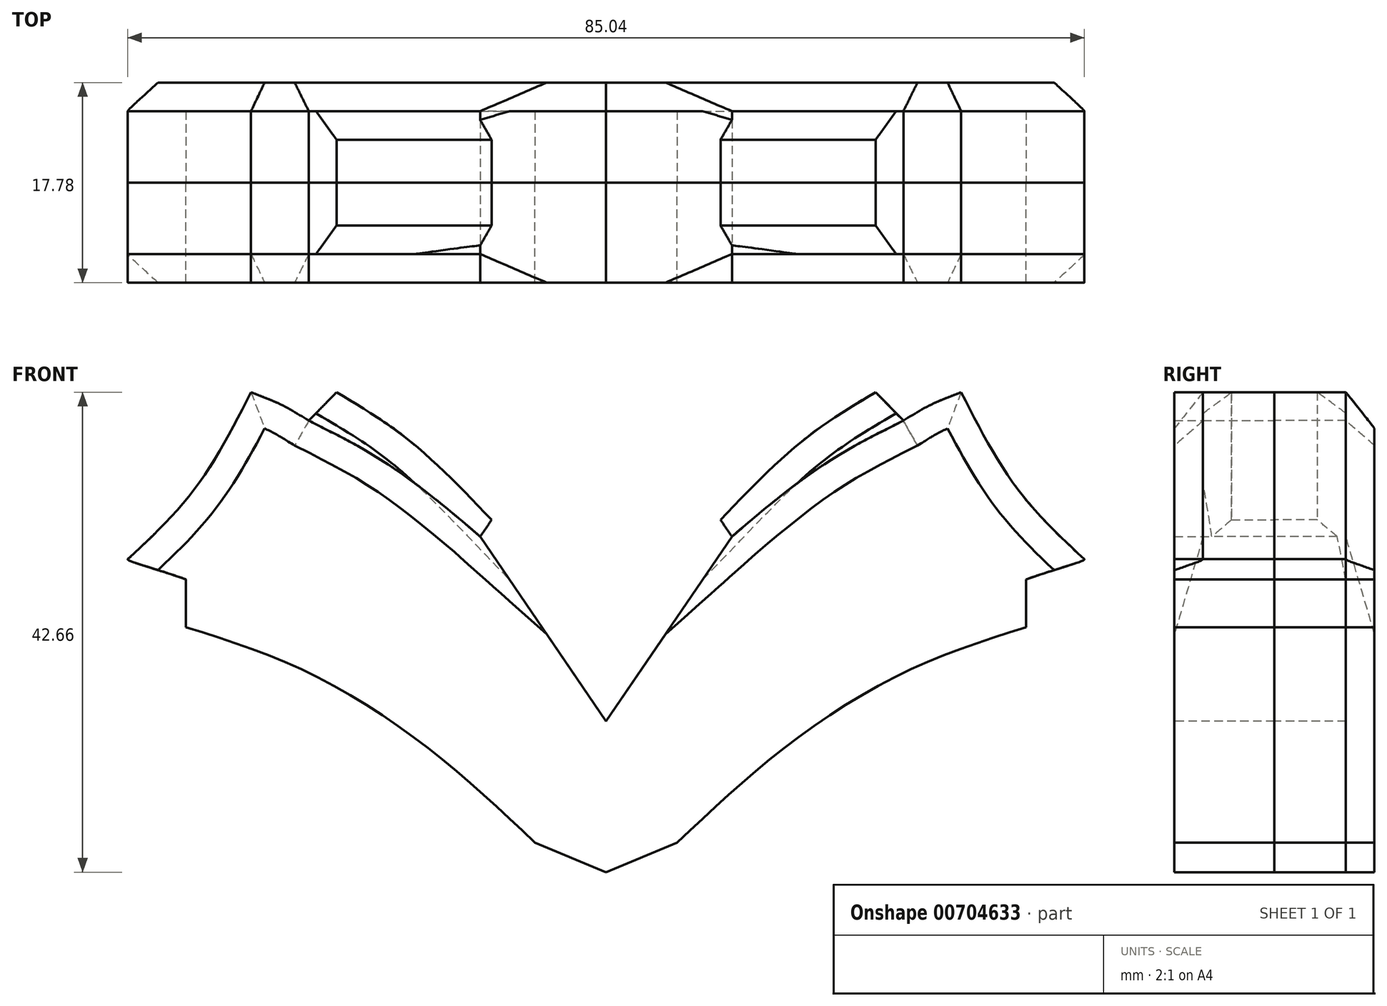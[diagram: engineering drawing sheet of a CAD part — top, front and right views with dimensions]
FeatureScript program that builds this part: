
annotation { "Feature Type Name" : "Feature", "Feature Type Description" : "" }
export const myFeature = defineFeature(function(context is Context, id is Id, definition is map)
    precondition{}
    {
        {
            var Q0;
            Q0=qCreatedBy(makeId("Front.planeOp"),FACE);
            var sketch = newSketch(context, id + "F0", { "sketchPlane" : qUnion([Q0])});
            skFitSpline(sketch, "E0", {"points": [v(-18.66, -145.03) * mm, v(-12.41, -140.25) * mm, v(-7.43, -132.73) * mm], "startDerivative": vector(13.73, 8.78) * mm, "endDerivative": vector(8.77, 15.73) * mm});
            skFitSpline(sketch, "E1", {"points": [v(0, -156.5) * mm, v(-5.42, -154.99) * mm, v(-8.85, -151.2) * mm], "startDerivative": vector(-11.5, 1.7) * mm, "endDerivative": vector(-6.16, 8.95) * mm});
            skFitSpline(sketch, "E2", {"points": [v(-6.32, -27.2) * mm, v(-15.28, -19.21) * mm, v(-26.43, -12.1) * mm, v(-37.33, -8.05) * mm], "startDerivative": vector(-25.96, 24.63) * mm, "endDerivative": vector(-33.62, 10.63) * mm});
            skFitSpline(sketch, "E3", {"points": [v(-37.33, -3.8) * mm, v(-39.84, -2.96) * mm, v(-42.51, -2.04) * mm, v(-42.5, -2) * mm], "startDerivative": vector(-4.66, 1.6) * mm, "endDerivative": vector(0.46, 0.6) * mm});
            skFitSpline(sketch, "E4", {"points": [v(-42.5, -2) * mm, v(-36.56, 4.25) * mm, v(-31.56, 12.84) * mm], "startDerivative": vector(12.98, 12.08) * mm, "endDerivative": vector(8.97, 17.54) * mm});
            skFitSpline(sketch, "E5", {"points": [v(-31.56, 12.84) * mm, v(-28.75, 11.67) * mm, v(-26.43, 10.32) * mm], "startDerivative": vector(5.62, -2.14) * mm, "endDerivative": vector(4.63, -2.93) * mm});
            skFitSpline(sketch, "E6", {"points": [v(-23.95, 12.84) * mm, v(-17.54, 8.59) * mm, v(-10.17, 1.5) * mm], "startDerivative": vector(13.82, -8.22) * mm, "endDerivative": vector(13.74, -14.33) * mm});
            skLineSegment(sketch, "E7", {"start": v(-10.17, 1.5) * mm, "end": v(0, 17.06) * mm});
            skLineSegment(sketch, "E8", {"start": v(0, 17.06) * mm, "end": v(0, 9.54) * mm});
            skLineSegment(sketch, "E9", {"start": v(0, 9.54) * mm, "end": v(0, 17.06) * mm});
            skLineSegment(sketch, "E10", {"start": v(-37.33, -3.8) * mm, "end": v(-37.33, -8.05) * mm});
            skLineSegment(sketch, "E11", {"start": v(-23.95, 12.84) * mm, "end": v(-26.43, 10.32) * mm});
            skLineSegment(sketch, "E12", {"start": v(-6.32, -27.2) * mm, "end": v(0, -29.82) * mm});
            skLineSegment(sketch, "E13", {"start": v(0, -29.82) * mm, "end": v(-6.32, -27.2) * mm});
            skLineSegment(sketch, "E14", {"start": v(-7.43, -132.73) * mm, "end": v(-4.54, -130.41) * mm});
            skLineSegment(sketch, "E15", {"start": v(-4.54, -130.41) * mm, "end": v(0, -130.41) * mm});
            skLineSegment(sketch, "E16", {"start": v(0, -130.41) * mm, "end": v(-4.54, -130.41) * mm});
            skLineSegment(sketch, "E17", {"start": v(-8.85, -151.2) * mm, "end": v(-10.72, -152.9) * mm});
            skLineSegment(sketch, "E18", {"start": v(-10.72, -152.9) * mm, "end": v(-18.24, -148.4) * mm});
            skLineSegment(sketch, "E19", {"start": v(-18.24, -148.4) * mm, "end": v(-18.66, -145.03) * mm});
            skLineSegment(sketch, "E20.MirrorCS", {"start": v(10.17, 1.5) * mm, "end": v(0, 17.06) * mm});
            skFitSpline(sketch, "E21.MirrorCS", {"points": [v(23.95, 12.84) * mm, v(17.54, 8.59) * mm, v(10.17, 1.5) * mm], "startDerivative": vector(-13.82, -8.22) * mm, "endDerivative": vector(-13.74, -14.33) * mm});
            skLineSegment(sketch, "E22.MirrorCS", {"start": v(23.95, 12.84) * mm, "end": v(26.43, 10.32) * mm});
            skFitSpline(sketch, "E23.MirrorCS", {"points": [v(31.56, 12.84) * mm, v(28.75, 11.67) * mm, v(26.43, 10.32) * mm], "startDerivative": vector(-5.62, -2.14) * mm, "endDerivative": vector(-4.63, -2.93) * mm});
            skFitSpline(sketch, "E24.MirrorCS", {"points": [v(42.5, -2) * mm, v(36.56, 4.25) * mm, v(31.56, 12.84) * mm], "startDerivative": vector(-12.98, 12.08) * mm, "endDerivative": vector(-8.97, 17.54) * mm});
            skFitSpline(sketch, "E25.MirrorCS", {"points": [v(37.33, -3.8) * mm, v(39.84, -2.96) * mm, v(42.51, -2.04) * mm, v(42.5, -2) * mm], "startDerivative": vector(4.66, 1.6) * mm, "endDerivative": vector(-0.46, 0.6) * mm});
            skLineSegment(sketch, "E26.MirrorCS", {"start": v(37.33, -3.8) * mm, "end": v(37.33, -8.05) * mm});
            skFitSpline(sketch, "E27.MirrorCS", {"points": [v(6.32, -27.2) * mm, v(15.28, -19.21) * mm, v(26.43, -12.1) * mm, v(37.33, -8.05) * mm], "startDerivative": vector(25.96, 24.63) * mm, "endDerivative": vector(33.62, 10.63) * mm});
            skLineSegment(sketch, "E28.MirrorCS", {"start": v(6.32, -27.2) * mm, "end": v(0, -29.82) * mm});
            skLineSegment(sketch, "E29.MirrorCS", {"start": v(0, -130.41) * mm, "end": v(4.54, -130.41) * mm});
            skLineSegment(sketch, "E30.MirrorCS", {"start": v(7.43, -132.73) * mm, "end": v(4.54, -130.41) * mm});
            skFitSpline(sketch, "E31.MirrorCS", {"points": [v(18.66, -145.03) * mm, v(12.41, -140.25) * mm, v(7.43, -132.73) * mm], "startDerivative": vector(-13.73, 8.78) * mm, "endDerivative": vector(-8.77, 15.73) * mm});
            skLineSegment(sketch, "E32.MirrorCS", {"start": v(18.24, -148.4) * mm, "end": v(18.66, -145.03) * mm});
            skLineSegment(sketch, "E33.MirrorCS", {"start": v(10.72, -152.9) * mm, "end": v(18.24, -148.4) * mm});
            skLineSegment(sketch, "E34.MirrorCS", {"start": v(8.85, -151.2) * mm, "end": v(10.72, -152.9) * mm});
            skFitSpline(sketch, "E35.MirrorCS", {"points": [v(0, -156.5) * mm, v(5.42, -154.99) * mm, v(8.85, -151.2) * mm], "startDerivative": vector(11.5, 1.7) * mm, "endDerivative": vector(6.16, 8.95) * mm});
            skSolve(sketch);
        }
        {
            var Q0;
            Q0=makeQuery(id+"F0.imprint","IMPRINT",FACE,{"disambiguationData":[TD([[makeQuery(id+"F0.imprint","IMPRINT",EDGE,{"derivedFrom":sQuery(id+"F0.wireOp",EDGE,"E2")}),-1.0]])]});
            var Q1;
            Q1=makeQuery(id+"F0.imprint","IMPRINT",FACE,{"disambiguationData":[TD([[makeQuery(id+"F0.imprint","IMPRINT",EDGE,{"derivedFrom":sQuery(id+"F0.wireOp",EDGE,"E0")}),-1.0]])]});
            extrude(context, id + "F1", {"entities" : qUnion([Q0, Q1]), "depth" : 6.35 * mm, "offsetDistance" : 25.4 * mm});
        }
        {
            var Q0;
            Q0=makeQuery(id+"F1.opExtrude","CAP_FACE",FACE,{"disambiguationData":[OSD([sQuery(id+"F0.wireOp",EDGE,"E2"),sQuery(id+"F0.wireOp",EDGE,"E3"),sQuery(id+"F0.wireOp",EDGE,"E4"),sQuery(id+"F0.wireOp",EDGE,"E5"),sQuery(id+"F0.wireOp",EDGE,"E6"),sQuery(id+"F0.wireOp",EDGE,"E7"),sQuery(id+"F0.wireOp",EDGE,"E10"),sQuery(id+"F0.wireOp",EDGE,"E11"),sQuery(id+"F0.wireOp",EDGE,"E13"),sQuery(id+"F0.wireOp",EDGE,"E20.MirrorCS"),sQuery(id+"F0.wireOp",EDGE,"E21.MirrorCS"),sQuery(id+"F0.wireOp",EDGE,"E22.MirrorCS"),sQuery(id+"F0.wireOp",EDGE,"E23.MirrorCS"),sQuery(id+"F0.wireOp",EDGE,"E24.MirrorCS"),sQuery(id+"F0.wireOp",EDGE,"E25.MirrorCS"),sQuery(id+"F0.wireOp",EDGE,"E26.MirrorCS"),sQuery(id+"F0.wireOp",EDGE,"E27.MirrorCS"),sQuery(id+"F0.wireOp",EDGE,"E28.MirrorCS")])],"isStart":true});
            var Q1;
            Q1=makeQuery(id+"F1.opExtrude","CAP_FACE",FACE,{"disambiguationData":[OSD([sQuery(id+"F0.wireOp",EDGE,"E0"),sQuery(id+"F0.wireOp",EDGE,"E1"),sQuery(id+"F0.wireOp",EDGE,"E14"),sQuery(id+"F0.wireOp",EDGE,"E16"),sQuery(id+"F0.wireOp",EDGE,"E17"),sQuery(id+"F0.wireOp",EDGE,"E18"),sQuery(id+"F0.wireOp",EDGE,"E19"),sQuery(id+"F0.wireOp",EDGE,"E29.MirrorCS"),sQuery(id+"F0.wireOp",EDGE,"E30.MirrorCS"),sQuery(id+"F0.wireOp",EDGE,"E31.MirrorCS"),sQuery(id+"F0.wireOp",EDGE,"E32.MirrorCS"),sQuery(id+"F0.wireOp",EDGE,"E33.MirrorCS"),sQuery(id+"F0.wireOp",EDGE,"E34.MirrorCS"),sQuery(id+"F0.wireOp",EDGE,"E35.MirrorCS")])],"isStart":true});
            extrude(context, id + "F2", {"entities" : qUnion([Q0, Q1]), "depth" : 6.35 * mm, "offsetDistance" : 25.4 * mm});
        }
        {
            var Q0;
            Q0=makeQuery(id+"F1.opExtrude","CAP_FACE",FACE,{"disambiguationData":[OSD([sQuery(id+"F0.wireOp",EDGE,"E2"),sQuery(id+"F0.wireOp",EDGE,"E3"),sQuery(id+"F0.wireOp",EDGE,"E4"),sQuery(id+"F0.wireOp",EDGE,"E5"),sQuery(id+"F0.wireOp",EDGE,"E6"),sQuery(id+"F0.wireOp",EDGE,"E7"),sQuery(id+"F0.wireOp",EDGE,"E10"),sQuery(id+"F0.wireOp",EDGE,"E11"),sQuery(id+"F0.wireOp",EDGE,"E13"),sQuery(id+"F0.wireOp",EDGE,"E20.MirrorCS"),sQuery(id+"F0.wireOp",EDGE,"E21.MirrorCS"),sQuery(id+"F0.wireOp",EDGE,"E22.MirrorCS"),sQuery(id+"F0.wireOp",EDGE,"E23.MirrorCS"),sQuery(id+"F0.wireOp",EDGE,"E24.MirrorCS"),sQuery(id+"F0.wireOp",EDGE,"E25.MirrorCS"),sQuery(id+"F0.wireOp",EDGE,"E26.MirrorCS"),sQuery(id+"F0.wireOp",EDGE,"E27.MirrorCS"),sQuery(id+"F0.wireOp",EDGE,"E28.MirrorCS")])],"isStart":false});
            var sketch = newSketch(context, id + "F3", { "sketchPlane" : qUnion([Q0])});
            skFitSpline(sketch, "E36", {"points": [v(-26.43, 10.32) * mm, v(-20.88, 7.37) * mm, v(-15.82, 3.86) * mm, v(-11.19, 0) * mm, v(-9.86, -1.24) * mm], "startDerivative": vector(19.99, -10.01) * mm, "endDerivative": vector(7.2, -6.92) * mm});
            skLineSegment(sketch, "E37", {"start": v(-9.86, -1.24) * mm, "end": v(0, -16.46) * mm});
            skLineSegment(sketch, "E38.MirrorCS", {"start": v(9.86, -1.24) * mm, "end": v(0, -16.46) * mm});
            skFitSpline(sketch, "E39.MirrorCS", {"points": [v(26.43, 10.32) * mm, v(20.88, 7.37) * mm, v(15.82, 3.86) * mm, v(11.19, 0) * mm, v(9.86, -1.24) * mm], "startDerivative": vector(-19.99, -10.01) * mm, "endDerivative": vector(-7.2, -6.92) * mm});
            skLineSegment(sketch, "E40", {"start": v(-10.17, 1.5) * mm, "end": v(-11.19, 0) * mm});
            skLineSegment(sketch, "E41", {"start": v(10.17, 1.5) * mm, "end": v(11.19, 0) * mm});
            skSolve(sketch);
        }
        {
            var Q0;
            {var subQ7=sQuery(id+"F3.wireOp",EDGE,"E37");Q0=makeQuery(id+"F3.imprint","IMPRINT",FACE,{"disambiguationData":[TD([[makeQuery(id+"F3.imprint","IMPRINT",EDGE,{"derivedFrom":subQ7}),-1.0]])]});}
            var Q1;
            {var subQ3=sQuery(id+"F3.wireOp",EDGE,"E37");Q1=makeQuery(id+"F3.imprint","IMPRINT",FACE,{"disambiguationData":[TD([[makeQuery(id+"F3.imprint","IMPRINT",EDGE,{"derivedFrom":subQ3}),1.0]])]});}
            extrude(context, id + "F4", {"entities" : qUnion([Q0, Q1]), "operationType" : NewBodyOperationType.ADD, "depth" : 2.54 * mm, "offsetDistance" : 25.4 * mm});
        }
        {
            var Q0;
            Q0=makeQuery(id+"F4.opExtrude","CAP_FACE",FACE,{"disambiguationData":[OSD([sQuery(id+"F0.wireOp",EDGE,"E2"),sQuery(id+"F0.wireOp",EDGE,"E3"),sQuery(id+"F0.wireOp",EDGE,"E4"),sQuery(id+"F0.wireOp",EDGE,"E5"),sQuery(id+"F0.wireOp",EDGE,"E7"),sQuery(id+"F0.wireOp",EDGE,"E10"),sQuery(id+"F0.wireOp",EDGE,"E13"),sQuery(id+"F0.wireOp",EDGE,"E20.MirrorCS"),sQuery(id+"F0.wireOp",EDGE,"E23.MirrorCS"),sQuery(id+"F0.wireOp",EDGE,"E24.MirrorCS"),sQuery(id+"F0.wireOp",EDGE,"E25.MirrorCS"),sQuery(id+"F0.wireOp",EDGE,"E26.MirrorCS"),sQuery(id+"F0.wireOp",EDGE,"E27.MirrorCS"),sQuery(id+"F0.wireOp",EDGE,"E28.MirrorCS"),sQuery(id+"F3.wireOp",EDGE,"E36"),sQuery(id+"F3.wireOp",EDGE,"E39.MirrorCS"),sQuery(id+"F3.wireOp",EDGE,"E40"),sQuery(id+"F3.wireOp",EDGE,"E41")])],"isStart":false});
            extrude(context, id + "F5", {"entities" : qUnion([Q0]), "oppositeDirection" : true, "depth" : 17.78 * mm, "offsetDistance" : 25.4 * mm});
        }
        {
            var Q0;
            Q0=makeQuery(id+"F5.opExtrude","CAP_FACE",FACE,{"disambiguationData":[OSD([sQuery(id+"F0.wireOp",EDGE,"E2"),sQuery(id+"F0.wireOp",EDGE,"E3"),sQuery(id+"F0.wireOp",EDGE,"E4"),sQuery(id+"F0.wireOp",EDGE,"E5"),sQuery(id+"F0.wireOp",EDGE,"E7"),sQuery(id+"F0.wireOp",EDGE,"E10"),sQuery(id+"F0.wireOp",EDGE,"E13"),sQuery(id+"F0.wireOp",EDGE,"E20.MirrorCS"),sQuery(id+"F0.wireOp",EDGE,"E23.MirrorCS"),sQuery(id+"F0.wireOp",EDGE,"E24.MirrorCS"),sQuery(id+"F0.wireOp",EDGE,"E25.MirrorCS"),sQuery(id+"F0.wireOp",EDGE,"E26.MirrorCS"),sQuery(id+"F0.wireOp",EDGE,"E27.MirrorCS"),sQuery(id+"F0.wireOp",EDGE,"E28.MirrorCS"),sQuery(id+"F3.wireOp",EDGE,"E36"),sQuery(id+"F3.wireOp",EDGE,"E39.MirrorCS"),sQuery(id+"F3.wireOp",EDGE,"E40"),sQuery(id+"F3.wireOp",EDGE,"E41")])],"isStart":true});
            var sketch = newSketch(context, id + "F6", { "sketchPlane" : qUnion([Q0])});
            skLineSegment(sketch, "E42", {"start": v(-11.19, 0) * mm, "end": v(0, -16.42) * mm});
            skLineSegment(sketch, "E43", {"start": v(0, -16.42) * mm, "end": v(11.19, 0) * mm});
            skSolve(sketch);
        }
        {
            var Q0;
            Q0=makeQuery(id+"F6.imprint","IMPRINT",FACE,{"disambiguationData":[TD([[makeQuery(id+"F6.imprint","IMPRINT",EDGE,{"derivedFrom":sQuery(id+"F6.wireOp",EDGE,"E42")}),1.0]])]});
            extrude(context, id + "F7", {"entities" : qUnion([Q0]), "operationType" : NewBodyOperationType.REMOVE, "oppositeDirection" : true, "depth" : 25.4 * mm, "offsetDistance" : 25.4 * mm});
        }
        {
            var Q0;
            Q0=makeQuery(id+"F1.opExtrude","CAP_EDGE",EDGE,{"disambiguationData":[OSD([sQuery(id+"F0.wireOp",EDGE,"E6")])],"isStart":false});
            var Q1;
            Q1=makeQuery(id+"F1.opExtrude","CAP_EDGE",EDGE,{"disambiguationData":[OSD([sQuery(id+"F0.wireOp",EDGE,"E21.MirrorCS")])],"isStart":false});
            var Q2;
            Q2=makeQuery(id+"F2.opExtrude","CAP_EDGE",EDGE,{"disambiguationData":[OSD([sQuery(id+"F0.wireOp",EDGE,"E6")])],"isStart":false});
            var Q3;
            Q3=makeQuery(id+"F2.opExtrude","CAP_EDGE",EDGE,{"disambiguationData":[OSD([sQuery(id+"F0.wireOp",EDGE,"E21.MirrorCS")])],"isStart":false});
            chamfer(context, id + "F8", {"entities" : qUnion([Q0, Q1, Q2, Q3]), "width" : 2.54 * mm, "tangentPropagation" : true});
        }
        {
            var Q0;
            Q0=makeQuery(id+"F5.opExtrude","CAP_EDGE",EDGE,{"disambiguationData":[OSD([sQuery(id+"F3.wireOp",EDGE,"E36")])],"isStart":true});
            var Q1;
            Q1=makeQuery(id+"F5.opExtrude","CAP_EDGE",EDGE,{"disambiguationData":[OSD([sQuery(id+"F0.wireOp",EDGE,"E5")])],"isStart":true});
            var Q2;
            Q2=makeQuery(id+"F5.opExtrude","CAP_EDGE",EDGE,{"disambiguationData":[OSD([sQuery(id+"F0.wireOp",EDGE,"E4")])],"isStart":true});
            var Q3;
            Q3=makeQuery(id+"F5.opExtrude","CAP_EDGE",EDGE,{"disambiguationData":[OSD([sQuery(id+"F0.wireOp",EDGE,"E24.MirrorCS")])],"isStart":true});
            var Q4;
            Q4=makeQuery(id+"F5.opExtrude","CAP_EDGE",EDGE,{"disambiguationData":[OSD([sQuery(id+"F0.wireOp",EDGE,"E23.MirrorCS")])],"isStart":true});
            var Q5;
            Q5=makeQuery(id+"F5.opExtrude","CAP_EDGE",EDGE,{"disambiguationData":[OSD([sQuery(id+"F3.wireOp",EDGE,"E39.MirrorCS")])],"isStart":true});
            var Q6;
            Q6=makeQuery(id+"F5.opExtrude","CAP_EDGE",EDGE,{"disambiguationData":[OSD([sQuery(id+"F0.wireOp",EDGE,"E4")])],"isStart":false});
            var Q7;
            Q7=makeQuery(id+"F5.opExtrude","CAP_EDGE",EDGE,{"disambiguationData":[OSD([sQuery(id+"F0.wireOp",EDGE,"E5")])],"isStart":false});
            var Q8;
            Q8=makeQuery(id+"F5.opExtrude","CAP_EDGE",EDGE,{"disambiguationData":[OSD([sQuery(id+"F3.wireOp",EDGE,"E36")])],"isStart":false});
            var Q9;
            Q9=makeQuery(id+"F5.opExtrude","CAP_EDGE",EDGE,{"disambiguationData":[OSD([sQuery(id+"F3.wireOp",EDGE,"E39.MirrorCS")])],"isStart":false});
            var Q10;
            Q10=makeQuery(id+"F5.opExtrude","CAP_EDGE",EDGE,{"disambiguationData":[OSD([sQuery(id+"F0.wireOp",EDGE,"E23.MirrorCS")])],"isStart":false});
            var Q11;
            Q11=makeQuery(id+"F5.opExtrude","CAP_EDGE",EDGE,{"disambiguationData":[OSD([sQuery(id+"F0.wireOp",EDGE,"E24.MirrorCS")])],"isStart":false});
            chamfer(context, id + "F9", {"entities" : qUnion([Q0, Q1, Q2, Q3, Q4, Q5, Q6, Q7, Q8, Q9, Q10, Q11]), "width" : 2.54 * mm, "tangentPropagation" : true});
        }
        {
            var Q0;
            Q0=makeQuery(id+"F2.opExtrude","SWEPT_BODY",BODY,{"disambiguationData":[OSD([sQuery(id+"F0.wireOp",EDGE,"E0"),sQuery(id+"F0.wireOp",EDGE,"E1"),sQuery(id+"F0.wireOp",EDGE,"E14"),sQuery(id+"F0.wireOp",EDGE,"E16"),sQuery(id+"F0.wireOp",EDGE,"E17"),sQuery(id+"F0.wireOp",EDGE,"E18"),sQuery(id+"F0.wireOp",EDGE,"E19"),sQuery(id+"F0.wireOp",EDGE,"E29.MirrorCS"),sQuery(id+"F0.wireOp",EDGE,"E30.MirrorCS"),sQuery(id+"F0.wireOp",EDGE,"E31.MirrorCS"),sQuery(id+"F0.wireOp",EDGE,"E32.MirrorCS"),sQuery(id+"F0.wireOp",EDGE,"E33.MirrorCS"),sQuery(id+"F0.wireOp",EDGE,"E34.MirrorCS"),sQuery(id+"F0.wireOp",EDGE,"E35.MirrorCS")])]});
            var Q1;
            Q1=makeQuery(id+"F1.opExtrude","SWEPT_BODY",BODY,{"disambiguationData":[OSD([sQuery(id+"F0.wireOp",EDGE,"E0"),sQuery(id+"F0.wireOp",EDGE,"E1"),sQuery(id+"F0.wireOp",EDGE,"E14"),sQuery(id+"F0.wireOp",EDGE,"E16"),sQuery(id+"F0.wireOp",EDGE,"E17"),sQuery(id+"F0.wireOp",EDGE,"E18"),sQuery(id+"F0.wireOp",EDGE,"E19"),sQuery(id+"F0.wireOp",EDGE,"E29.MirrorCS"),sQuery(id+"F0.wireOp",EDGE,"E30.MirrorCS"),sQuery(id+"F0.wireOp",EDGE,"E31.MirrorCS"),sQuery(id+"F0.wireOp",EDGE,"E32.MirrorCS"),sQuery(id+"F0.wireOp",EDGE,"E33.MirrorCS"),sQuery(id+"F0.wireOp",EDGE,"E34.MirrorCS"),sQuery(id+"F0.wireOp",EDGE,"E35.MirrorCS")])]});
            deleteBodies(context, id + "F10", {"entities" : qUnion([Q0, Q1])});
        }
    });
